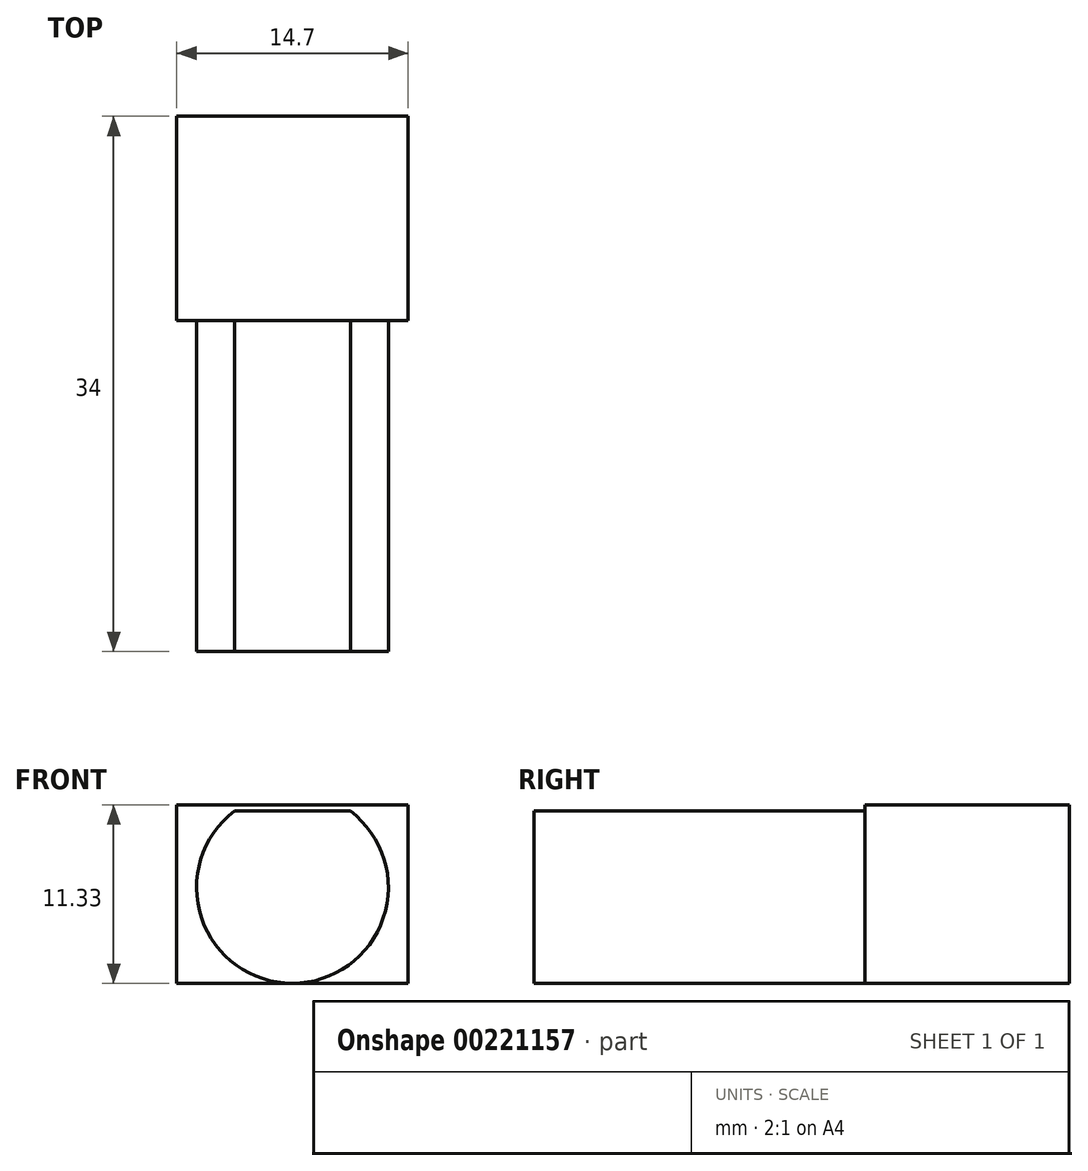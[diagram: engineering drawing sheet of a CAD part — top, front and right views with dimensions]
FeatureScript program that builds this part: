
annotation { "Feature Type Name" : "Feature", "Feature Type Description" : "" }
export const myFeature = defineFeature(function(context is Context, id is Id, definition is map)
    precondition{}
    {
        {
            var Q0;
            Q0=qCreatedBy(makeId("Top.planeOp"),FACE);
            var sketch = newSketch(context, id + "F0", { "sketchPlane" : qUnion([Q0])});
            skLineSegment(sketch, "E0.bottom", {"start": v(-28.55, 20.58) * mm, "end": v(-13.85, 20.58) * mm});
            skLineSegment(sketch, "E0.top", {"start": v(-28.55, 7.58) * mm, "end": v(-13.85, 7.58) * mm});
            skLineSegment(sketch, "E0.left", {"start": v(-28.55, 20.58) * mm, "end": v(-28.55, 7.58) * mm});
            skLineSegment(sketch, "E0.right", {"start": v(-13.85, 20.58) * mm, "end": v(-13.85, 7.58) * mm});
            skSolve(sketch);
        }
        {
            var Q0;
            Q0=makeQuery(id+"F0.imprint","IMPRINT",FACE,{"disambiguationData":[TD([[makeQuery(id+"F0.imprint","IMPRINT",EDGE,{"derivedFrom":sQuery(id+"F0.wireOp",EDGE,"E0.bottom")}),-1.0]])]});
            extrude(context, id + "F1", {"entities" : qUnion([Q0]), "depth" : 11.33 * mm});
        }
        {
            var Q0;
            Q0=makeQuery(id+"F1.opExtrude","SWEPT_FACE",FACE,{"disambiguationData":[OSD([sQuery(id+"F0.wireOp",EDGE,"E0.bottom")])]});
            var sketch = newSketch(context, id + "F2", { "sketchPlane" : qUnion([Q0])});
            skCircle(sketch, "E1", {"center": v(21.2, 6.1) * mm, "radius": 6.1 * mm, "construction": true});
            skLineSegment(sketch, "E2", {"start": v(17.52, 10.94) * mm, "end": v(24.89, 10.94) * mm});
            skPoint(sketch, "E3", {"position": v(21.2, 11.33) * mm});
            skArc(sketch, "E4", {"start": v(17.52, 10.94) * mm, "mid": v(21.2, 0) * mm, "end": v(24.89, 10.94) * mm});
            skSolve(sketch);
        }
        {
            var Q0;
            {var subQ0=sQuery(id+"F2.wireOp",EDGE,"E2");Q0=makeQuery(id+"F2.imprint","IMPRINT",FACE,{"disambiguationData":[TD([[makeQuery(id+"F2.imprint","IMPRINT",EDGE,{"derivedFrom":subQ0}),-1.0]])]});}
            extrude(context, id + "F3", {"entities" : qUnion([Q0]), "operationType" : NewBodyOperationType.ADD, "oppositeDirection" : true, "depth" : 34 * mm});
        }
    });
